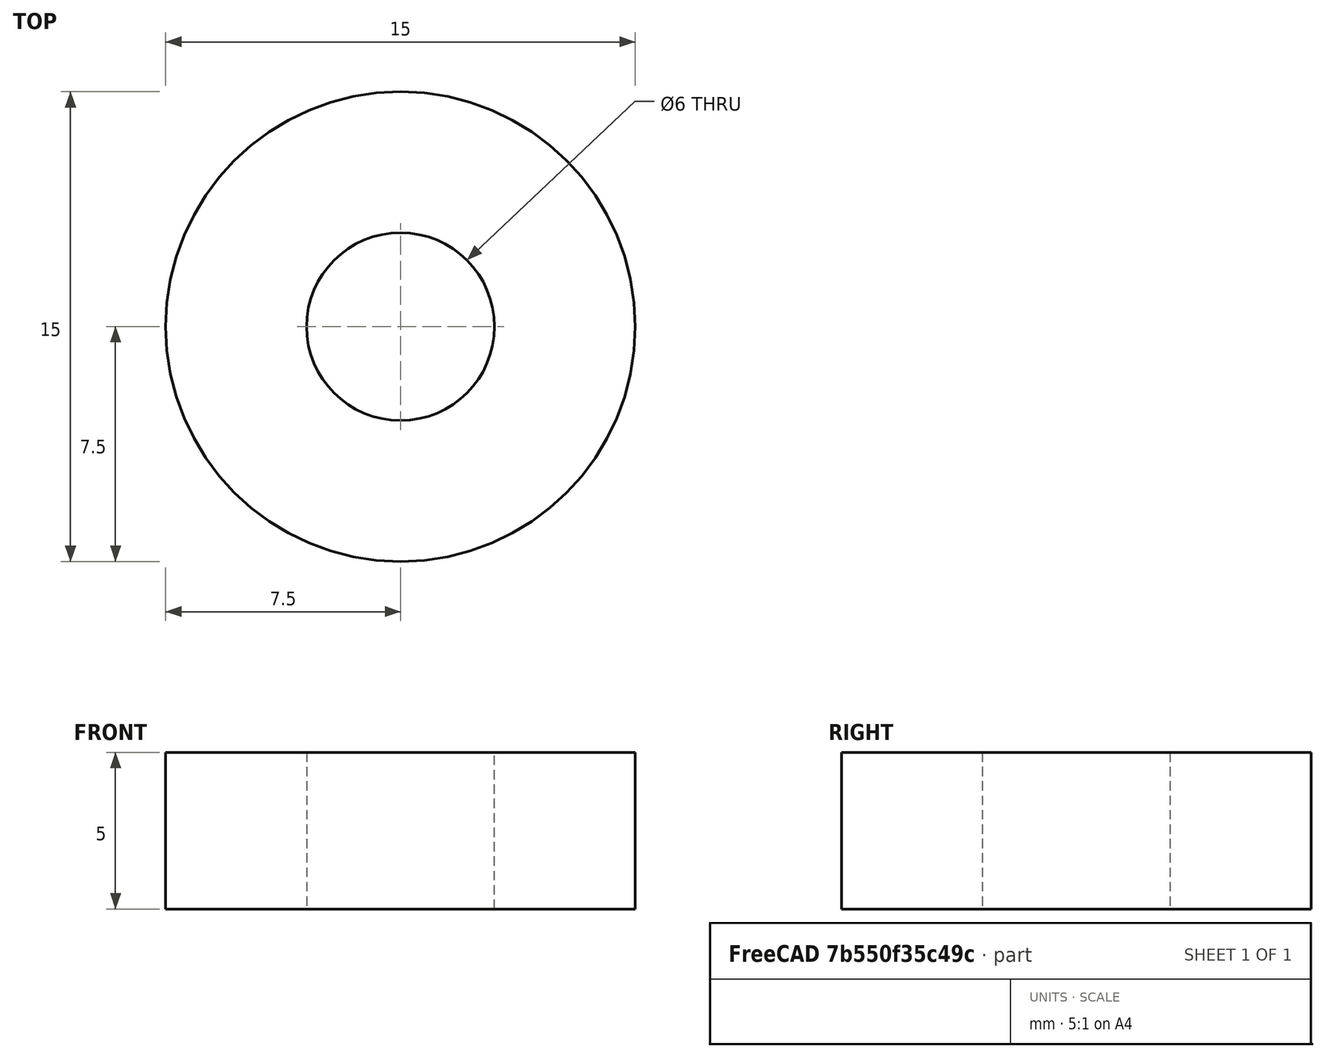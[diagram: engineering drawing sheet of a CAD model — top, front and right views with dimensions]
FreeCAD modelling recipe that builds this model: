
FCSTD DOCUMENT  (FreeCAD 1.0R39109 (Git))
Label: spacer
License: All rights reserved
LicenseURL: https://en.wikipedia.org/wiki/All_rights_reserved
objects: Sketcher::SketchObject×1, PartDesign::Pad×1, PartDesign::Body×1
note: 6 computed .brp shape members not serialized (recipe doc carries the construction recipe); baked Part::Feature solids carry a one-line shape summary decoded from their .brp

FEATURE [Sketcher::SketchObject] Sketch
  ArcFitTolerance = 1e-06
  AttachmentSupport = -> [XY_Plane]
  FullyConstrained = true
  MakeInternals = false
  MapMode = 5
  sketch-geometry (2):
    g0: Circle CenterX=0 CenterY=0 CenterZ=0 NormalX=0 NormalY=0 NormalZ=1 AngleXU=0 Radius=7.5
    g1: Circle CenterX=0 CenterY=0 CenterZ=0 NormalX=0 NormalY=0 NormalZ=1 AngleXU=0 Radius=3
  constraints (4):
    c: Diameter(g0) = 15
    c: Coincident(g0,g-1)
    c: Diameter(g1) = 6
    c: Coincident(g1,g0)
FEATURE [PartDesign::Pad] Pad
  Direction = (0,0,1)
  Length = 5
  Length2 = 10
  Profile = -> Sketch
  ReferenceAxis = -> Sketch [N_Axis]
  Refine = true
  Suppressed = false
  Type = 0
FEATURE [PartDesign::Body] Body
  AllowCompound = false
  Group = -> [Sketch,Pad]
  Origin = -> Origin
  Tip = -> Pad
